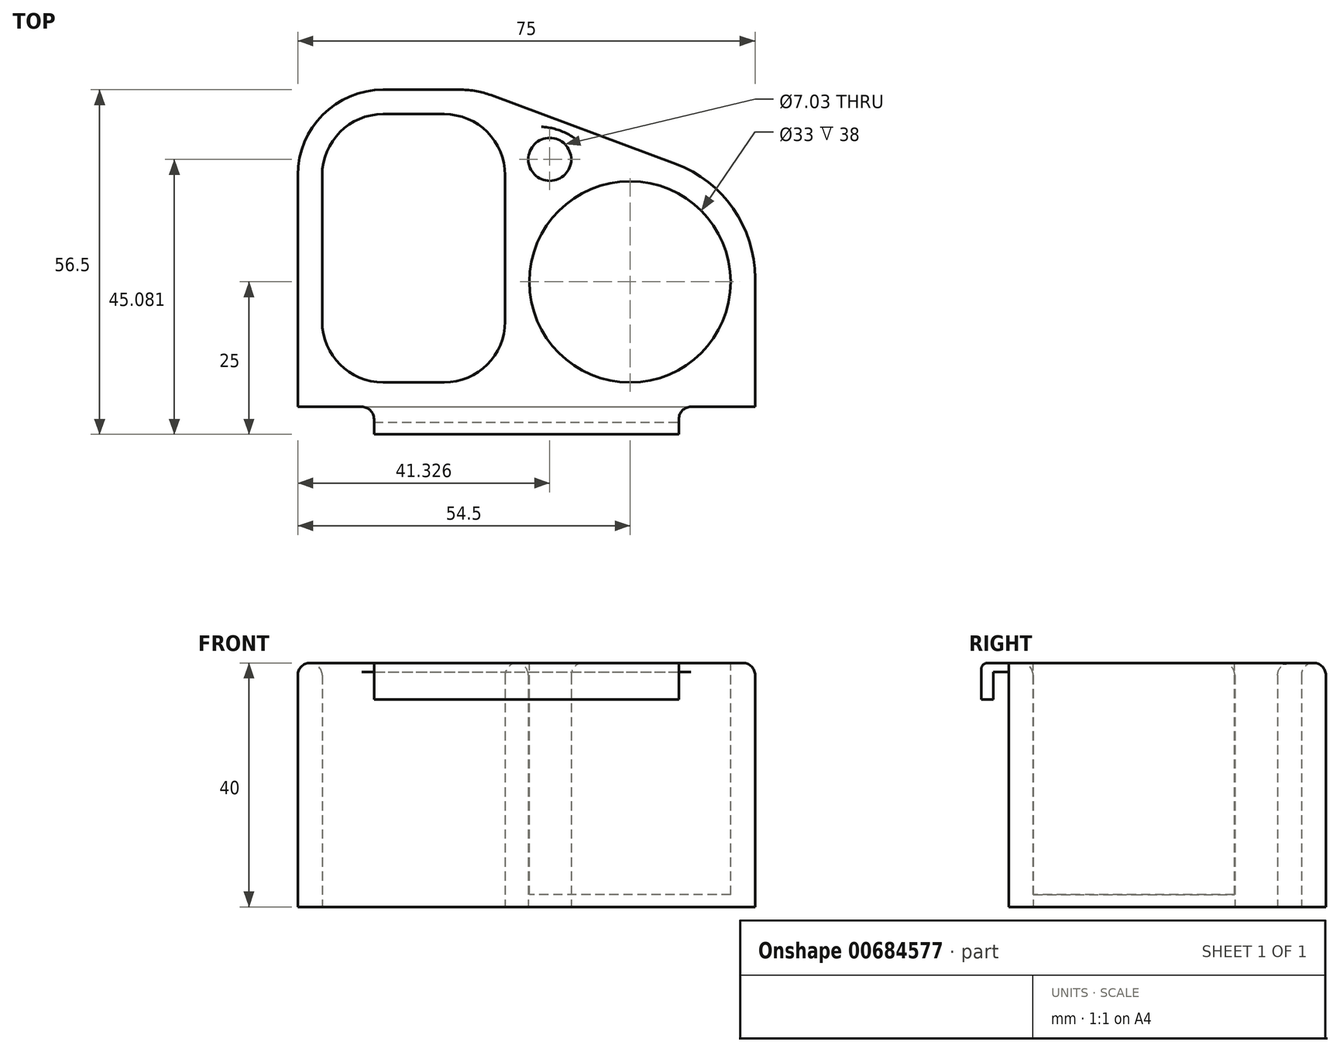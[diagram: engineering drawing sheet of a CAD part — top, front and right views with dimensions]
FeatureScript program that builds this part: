
annotation { "Feature Type Name" : "Feature", "Feature Type Description" : "" }
export const myFeature = defineFeature(function(context is Context, id is Id, definition is map)
    precondition{}
    {
        {
            var Q0;
            Q0=qCreatedBy(makeId("Top.planeOp"),FACE);
            var sketch = newSketch(context, id + "F0", { "sketchPlane" : qUnion([Q0])});
            skLineSegment(sketch, "E0", {"start": v(0, 0) * mm, "end": v(12.5, 0) * mm});
            skLineSegment(sketch, "E1", {"start": v(12.5, 0) * mm, "end": v(12.5, -4.5) * mm});
            skLineSegment(sketch, "E2", {"start": v(12.5, -4.5) * mm, "end": v(62.5, -4.5) * mm});
            skLineSegment(sketch, "E3", {"start": v(62.5, -4.5) * mm, "end": v(62.5, 0) * mm});
            skLineSegment(sketch, "E4", {"start": v(62.5, 0) * mm, "end": v(75, 0) * mm});
            skLineSegment(sketch, "E5", {"start": v(75, 0) * mm, "end": v(75, 21.1) * mm});
            skLineSegment(sketch, "E6", {"start": v(61.98, 39.85) * mm, "end": v(31.7, 51.12) * mm});
            skLineSegment(sketch, "E7", {"start": v(26.81, 52) * mm, "end": v(14, 52) * mm});
            skLineSegment(sketch, "E8", {"start": v(0, 38) * mm, "end": v(0, 0) * mm});
            skLineSegment(sketch, "E9.bottom", {"start": v(14, 48) * mm, "end": v(24, 48) * mm});
            skLineSegment(sketch, "E9.top", {"start": v(14, 4) * mm, "end": v(24, 4) * mm});
            skLineSegment(sketch, "E9.left", {"start": v(4, 38) * mm, "end": v(4, 14) * mm});
            skLineSegment(sketch, "E9.right", {"start": v(34, 38) * mm, "end": v(34, 14) * mm});
            skPoint(sketch, "E10.visualSharp", {"position": v(4, 48) * mm});
            skArc(sketch, "E10.filletArc", {"start": v(14, 48) * mm, "mid": v(6.93, 45.07) * mm, "end": v(4, 38) * mm});
            skPoint(sketch, "E11.visualSharp", {"position": v(34, 48) * mm});
            skArc(sketch, "E11.filletArc", {"start": v(34, 38) * mm, "mid": v(31.07, 45.07) * mm, "end": v(24, 48) * mm});
            skPoint(sketch, "E12.visualSharp", {"position": v(34, 4) * mm});
            skArc(sketch, "E12.filletArc", {"start": v(24, 4) * mm, "mid": v(31.07, 6.93) * mm, "end": v(34, 14) * mm});
            skPoint(sketch, "E13.visualSharp", {"position": v(4, 4) * mm});
            skArc(sketch, "E13.filletArc", {"start": v(4, 14) * mm, "mid": v(6.93, 6.93) * mm, "end": v(14, 4) * mm});
            skPoint(sketch, "E14.visualSharp", {"position": v(0, 52) * mm});
            skArc(sketch, "E14.filletArc", {"start": v(14, 52) * mm, "mid": v(4.1, 47.9) * mm, "end": v(0, 38) * mm});
            skCircle(sketch, "E15", {"center": v(54.5, 20.5) * mm, "radius": 16.5 * mm});
            skPoint(sketch, "E16.visualSharp", {"position": v(29.33, 52) * mm});
            skArc(sketch, "E16.filletArc", {"start": v(31.7, 51.12) * mm, "mid": v(29.3, 51.78) * mm, "end": v(26.81, 52) * mm});
            skPoint(sketch, "E17.visualSharp", {"position": v(75, 35) * mm});
            skArc(sketch, "E17.filletArc", {"start": v(75, 21.1) * mm, "mid": v(71.42, 32.52) * mm, "end": v(61.98, 39.85) * mm});
            skCircle(sketch, "E18", {"center": v(41.33, 40.58) * mm, "radius": 3.52 * mm});
            skSolve(sketch);
        }
        {
            var Q0;
            Q0=makeQuery(id+"F0.imprint","IMPRINT",FACE,{"disambiguationData":[TD([[makeQuery(id+"F0.imprint","IMPRINT",EDGE,{"derivedFrom":sQuery(id+"F0.wireOp",EDGE,"E0")}),1.0]])]});
            var Q1;
            Q1=makeQuery(id+"F0.imprint","IMPRINT",FACE,{"disambiguationData":[TD([[makeQuery(id+"F0.imprint","IMPRINT",EDGE,{"derivedFrom":sQuery(id+"F0.wireOp",EDGE,"E15")}),1.0]])]});
            extrude(context, id + "F1", {"entities" : qUnion([Q0, Q1]), "depth" : 40 * mm, "offsetDistance" : 25 * mm});
        }
        {
            var Q0;
            Q0=makeQuery(id+"F1.opExtrude","CAP_FACE",FACE,{"disambiguationData":[OSD([sQuery(id+"F0.wireOp",EDGE,"E0"),sQuery(id+"F0.wireOp",EDGE,"E1"),sQuery(id+"F0.wireOp",EDGE,"E2"),sQuery(id+"F0.wireOp",EDGE,"E3"),sQuery(id+"F0.wireOp",EDGE,"E4"),sQuery(id+"F0.wireOp",EDGE,"E5"),sQuery(id+"F0.wireOp",EDGE,"E6"),sQuery(id+"F0.wireOp",EDGE,"E7"),sQuery(id+"F0.wireOp",EDGE,"E8"),sQuery(id+"F0.wireOp",EDGE,"E9.bottom"),sQuery(id+"F0.wireOp",EDGE,"E9.top"),sQuery(id+"F0.wireOp",EDGE,"E9.left"),sQuery(id+"F0.wireOp",EDGE,"E9.right"),sQuery(id+"F0.wireOp",EDGE,"E10.filletArc"),sQuery(id+"F0.wireOp",EDGE,"E11.filletArc"),sQuery(id+"F0.wireOp",EDGE,"E12.filletArc"),sQuery(id+"F0.wireOp",EDGE,"E13.filletArc"),sQuery(id+"F0.wireOp",EDGE,"E14.filletArc"),sQuery(id+"F0.wireOp",EDGE,"E16.filletArc"),sQuery(id+"F0.wireOp",EDGE,"E17.filletArc"),sQuery(id+"F0.wireOp",EDGE,"E18")])],"isStart":false});
            var sketch = newSketch(context, id + "F2", { "sketchPlane" : qUnion([Q0])});
            skCircle(sketch, "E19", {"center": v(54.5, 20.5) * mm, "radius": 16.5 * mm});
            skSolve(sketch);
        }
        {
            var Q0;
            Q0=makeQuery(id+"F2.imprint","IMPRINT",FACE,{"disambiguationData":[TD([[makeQuery(id+"F2.imprint","IMPRINT",EDGE,{"derivedFrom":sQuery(id+"F2.wireOp",EDGE,"E19")}),1.0]])]});
            extrude(context, id + "F3", {"entities" : qUnion([Q0]), "operationType" : NewBodyOperationType.REMOVE, "oppositeDirection" : true, "depth" : 38 * mm, "offsetDistance" : 25 * mm});
        }
        {
            var Q0;
            Q0=makeQuery(id+"F1.opExtrude","SWEPT_FACE",FACE,{"disambiguationData":[OSD([sQuery(id+"F0.wireOp",EDGE,"E2")])]});
            var sketch = newSketch(context, id + "F4", { "sketchPlane" : qUnion([Q0])});
            skLineSegment(sketch, "E20.bottom", {"start": v(12.5, 0) * mm, "end": v(62.5, 0) * mm});
            skLineSegment(sketch, "E20.top", {"start": v(12.5, 34) * mm, "end": v(62.5, 34) * mm});
            skLineSegment(sketch, "E20.left", {"start": v(12.5, 0) * mm, "end": v(12.5, 34) * mm});
            skLineSegment(sketch, "E20.right", {"start": v(62.5, 0) * mm, "end": v(62.5, 34) * mm});
            skSolve(sketch);
        }
        {
            var Q0;
            Q0=makeQuery(id+"F4.imprint","IMPRINT",FACE,{"disambiguationData":[TD([[makeQuery(id+"F4.imprint","IMPRINT",EDGE,{"derivedFrom":sQuery(id+"F4.wireOp",EDGE,"E20.bottom")}),1.0]])]});
            extrude(context, id + "F5", {"entities" : qUnion([Q0]), "operationType" : NewBodyOperationType.REMOVE, "oppositeDirection" : true, "depth" : 4.5 * mm, "offsetDistance" : 25 * mm});
        }
        {
            var Q0;
            Q0=makeQuery(id+"F5.boolean.opBoolean","COPY",FACE,{"derivedFrom":makeQuery(id+"F5.opExtrude","SWEPT_FACE",FACE,{"disambiguationData":[OSD([sQuery(id+"F4.wireOp",EDGE,"E20.top")])]})});
            var sketch = newSketch(context, id + "F6", { "sketchPlane" : qUnion([Q0])});
            skLineSegment(sketch, "E21.bottom", {"start": v(12.5, 4.5) * mm, "end": v(62.5, 4.5) * mm});
            skLineSegment(sketch, "E21.top", {"start": v(12.5, 2.5) * mm, "end": v(62.5, 2.5) * mm});
            skLineSegment(sketch, "E21.left", {"start": v(12.5, 4.5) * mm, "end": v(12.5, 2.5) * mm});
            skLineSegment(sketch, "E21.right", {"start": v(62.5, 4.5) * mm, "end": v(62.5, 2.5) * mm});
            skSolve(sketch);
        }
        {
            var Q0;
            {var subQ0=sQuery(id+"F6.wireOp",EDGE,"E21.top");Q0=makeQuery(id+"F6.imprint","IMPRINT",FACE,{"disambiguationData":[TD([[makeQuery(id+"F6.imprint","IMPRINT",EDGE,{"derivedFrom":subQ0}),-1.0]])]});}
            extrude(context, id + "F7", {"entities" : qUnion([Q0]), "operationType" : NewBodyOperationType.REMOVE, "oppositeDirection" : true, "depth" : 4.5 * mm, "offsetDistance" : 25 * mm});
        }
        {
            var Q0;
            Q0=makeQuery(id+"F3.boolean.opBoolean","COPY",EDGE,{"derivedFrom":makeQuery(id+"F3.opExtrude","CAP_EDGE",EDGE,{"disambiguationData":[OSD([sQuery(id+"F2.wireOp",EDGE,"E19")])],"isStart":true})});
            var Q1;
            Q1=makeQuery(id+"F1.opExtrude","CAP_EDGE",EDGE,{"disambiguationData":[OSD([sQuery(id+"F0.wireOp",EDGE,"E9.right")])],"isStart":false});
            var Q2;
            Q2=makeQuery(id+"F1.opExtrude","CAP_EDGE",EDGE,{"disambiguationData":[OSD([sQuery(id+"F0.wireOp",EDGE,"E18")])],"isStart":false});
            var Q3;
            Q3=makeQuery(id+"F1.opExtrude","CAP_EDGE",EDGE,{"disambiguationData":[OSD([sQuery(id+"F0.wireOp",EDGE,"E6")])],"isStart":false});
            var Q4;
            Q4=makeQuery(id+"F1.opExtrude","SWEPT_EDGE",EDGE,{"disambiguationData":[OSD([sQuery(id+"F0.wireOp",EDGE,"E0"),sQuery(id+"F0.wireOp",EDGE,"E1")])]});
            var Q5;
            Q5=makeQuery(id+"F1.opExtrude","SWEPT_EDGE",EDGE,{"disambiguationData":[OSD([sQuery(id+"F0.wireOp",EDGE,"E3"),sQuery(id+"F0.wireOp",EDGE,"E4")])]});
            fillet(context, id + "F8", {"entities" : qUnion([Q0, Q1, Q2, Q3, Q4, Q5]), "radius" : 2 * mm, "tangentPropagation" : true, "allowEdgeOverflow" : false});
        }
        {
            var Q0;
            Q0=makeQuery(id+"F1.opExtrude","CAP_EDGE",EDGE,{"disambiguationData":[OSD([sQuery(id+"F0.wireOp",EDGE,"E2")])],"isStart":false});
            fillet(context, id + "F9", {"entities" : qUnion([Q0]), "radius" : 1 * mm, "tangentPropagation" : true, "allowEdgeOverflow" : false});
        }
    });
